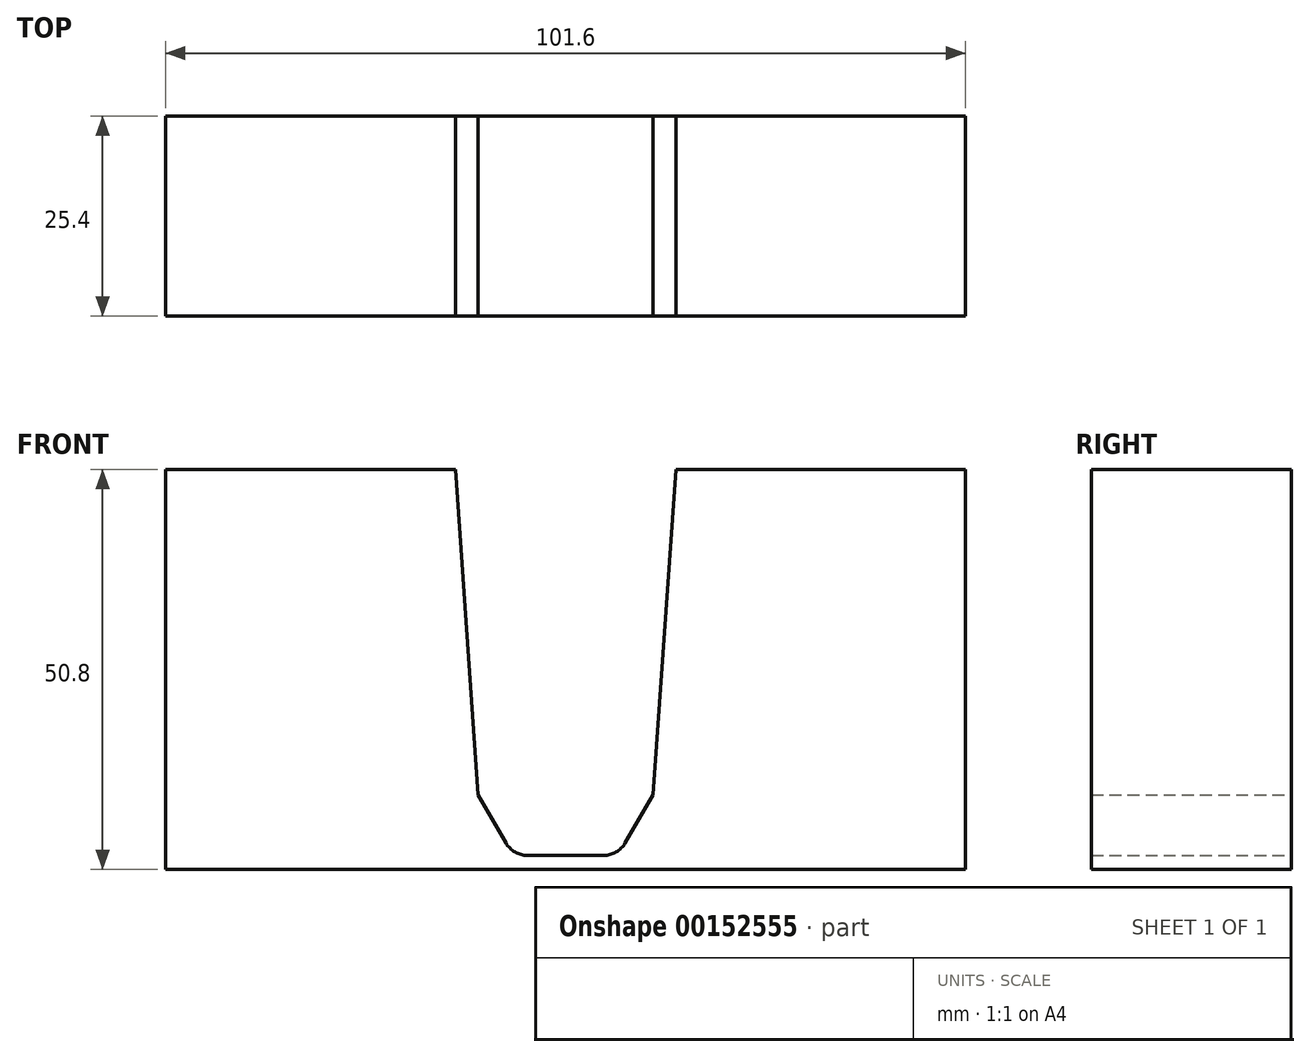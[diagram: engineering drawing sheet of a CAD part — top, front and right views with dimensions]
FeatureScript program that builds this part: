
annotation { "Feature Type Name" : "Feature", "Feature Type Description" : "" }
export const myFeature = defineFeature(function(context is Context, id is Id, definition is map)
    precondition{}
    {
        {
            var Q0;
            Q0=qCreatedBy(makeId("Front.planeOp"),FACE);
            var sketch = newSketch(context, id + "F0", { "sketchPlane" : qUnion([Q0])});
            skLineSegment(sketch, "E0", {"start": v(0, 0) * mm, "end": v(-50.8, 0) * mm});
            skLineSegment(sketch, "E1", {"start": v(-50.8, 0) * mm, "end": v(-50.8, 50.8) * mm});
            skLineSegment(sketch, "E2", {"start": v(-50.8, 50.8) * mm, "end": v(-14, 50.8) * mm});
            skLineSegment(sketch, "E3", {"start": v(-14, 50.8) * mm, "end": v(-11.11, 9.5) * mm});
            skLineSegment(sketch, "E4", {"start": v(-11.11, 9.5) * mm, "end": v(-7.58, 3.37) * mm});
            skLineSegment(sketch, "E5", {"start": v(-4.83, 1.78) * mm, "end": v(0, 1.78) * mm});
            skLineSegment(sketch, "E6", {"start": v(0, 1.78) * mm, "end": v(0, 0) * mm});
            skPoint(sketch, "E7.visualSharp", {"position": v(-6.66, 1.78) * mm});
            skArc(sketch, "E7.filletArc", {"start": v(-7.58, 3.37) * mm, "mid": v(-6.41, 2.2) * mm, "end": v(-4.83, 1.78) * mm});
            skSolve(sketch);
        }
        {
            var Q0;
            Q0=makeQuery(id+"F0.imprint","IMPRINT",FACE,{"disambiguationData":[TD([[makeQuery(id+"F0.imprint","IMPRINT",EDGE,{"derivedFrom":sQuery(id+"F0.wireOp",EDGE,"E0")}),-1.0]])]});
            extrude(context, id + "F1", {"entities" : qUnion([Q0]), "depth" : 25.4 * mm});
        }
        {
            var Q0;
            Q0=makeQuery(id+"F1.opExtrude","SWEPT_BODY",BODY,{"disambiguationData":[OSD([sQuery(id+"F0.wireOp",EDGE,"E0"),sQuery(id+"F0.wireOp",EDGE,"E1"),sQuery(id+"F0.wireOp",EDGE,"E2"),sQuery(id+"F0.wireOp",EDGE,"E3"),sQuery(id+"F0.wireOp",EDGE,"E4"),sQuery(id+"F0.wireOp",EDGE,"E5"),sQuery(id+"F0.wireOp",EDGE,"E6"),sQuery(id+"F0.wireOp",EDGE,"E7.filletArc")])]});
            var Q1;
            Q1=qCreatedBy(makeId("Right.planeOp"),FACE);
            mirror(context, id + "F2", {"operationType" : NewBodyOperationType.ADD, "entities" : qUnion([Q0]), "mirrorPlane" : qUnion([Q1])});
        }
    });
